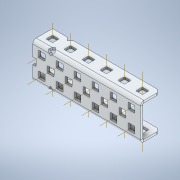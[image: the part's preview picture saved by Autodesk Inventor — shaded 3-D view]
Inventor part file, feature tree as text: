
AUTODESK INVENTOR PART (.ipt)
format: ipt  version: 2020 (Build 240168000, 168)  size: 1,193,472 bytes
history: native  units: in
note: dims shown in document units (in); Inventor stores cm internally (conversion verified against a paired STEP export)
features: other x33, plane x10, pattern_linear x4, split x4, sheet_metal_op x1
ambient origin geometry x8: Origin, YZ Plane, XZ Plane, XY Plane, X Axis, Y Axis, Z Axis, Center Point
bodies: Solid1 (feature_tree)
feature tree (52):
  other  "Work Axis1"
  pattern_linear  "Rectangular Pattern1"  Count1=6 Spacing1=0.5in
  other  "Work Axis72"
  pattern_linear  "Rectangular Pattern2"  Count1=6 Spacing1=0.5in
  pattern_linear  "Rectangular Pattern3"  Count1=6 Spacing1=0.5in
  other  "Work Axis141"
  pattern_linear  "Rectangular Pattern4"  Count1=5 Spacing1=0.5in
  plane  "Work Plane7"
  split  "Split1"
  plane  "Work Plane8"
  split  "Split2"
  plane  "Work Plane9"
  split  "Split3"
  plane  "Work Plane10"
  split  "Split4"
  plane  "Work Plane1"
  plane  "Work Plane2"
  other  "Work Point1"
  other  "Work Axis2"
  other  "Work Axis3"
  other  "Work Axis4"
  other  "Work Axis5"
  other  "Work Axis6"
  other  "Work Axis36"
  other  "Work Axis37"
  other  "Work Axis38"
  other  "Work Axis39"
  other  "Work Axis40"
  other  "Work Axis41"
  plane  "Work Plane3"
  plane  "Work Plane4"
  other  "Work Point2"
  other  "Work Axis71"
  other  "Work Point3"
  other  "Work Axis73"
  other  "Work Axis74"
  other  "Work Axis75"
  other  "Work Axis76"
  other  "Work Axis77"
  other  "Work Axis107"
  other  "Work Axis108"
  other  "Work Axis109"
  other  "Work Axis110"
  plane  "Work Plane5"
  plane  "Work Plane6"
  other  "Work Point4"
  other  "Work Axis142"
  other  "Work Axis143"
  other  "Work Axis144"
  other  "Work Axis145"
  other  "Work Axis175"
  sheet_metal_op  "Fold1"
